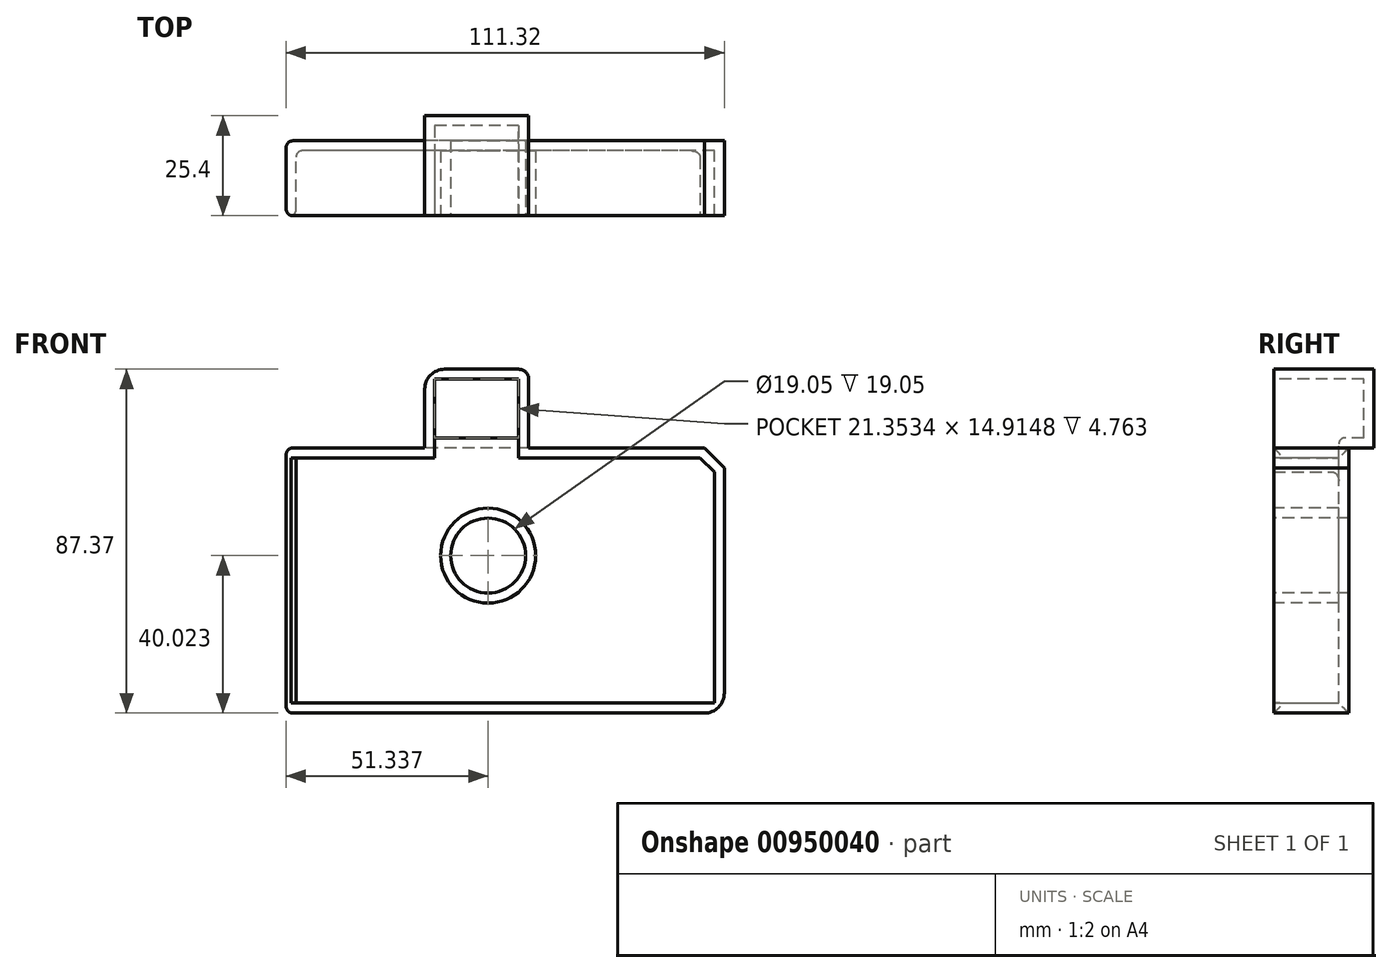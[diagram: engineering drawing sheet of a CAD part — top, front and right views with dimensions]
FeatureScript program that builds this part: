
annotation { "Feature Type Name" : "Feature", "Feature Type Description" : "" }
export const myFeature = defineFeature(function(context is Context, id is Id, definition is map)
    precondition{}
    {
        {
            var Q0;
            Q0=qCreatedBy(makeId("Front.planeOp"),FACE);
            var sketch = newSketch(context, id + "F0", { "sketchPlane" : qUnion([Q0])});
            skLineSegment(sketch, "E0.bottom", {"start": v(0, 21.6) * mm, "end": v(-111.32, 21.6) * mm});
            skLineSegment(sketch, "E0.top", {"start": v(0, 88.98) * mm, "end": v(-111.32, 88.98) * mm});
            skLineSegment(sketch, "E0.left", {"start": v(0, 21.6) * mm, "end": v(0, 88.98) * mm});
            skLineSegment(sketch, "E0.right", {"start": v(-111.32, 21.6) * mm, "end": v(-111.32, 88.98) * mm});
            skPoint(sketch, "E0.middle", {"position": v(-55.66, 55.3) * mm});
            skSolve(sketch);
        }
        {
            var Q0;
            Q0 = qSketchRegion(id + "F0", true);
            extrude(context, id + "F1", {"entities" : qUnion([Q0]), "depth" : 19.05 * mm, "offsetDistance" : 25.4 * mm});
        }
        {
            var Q0;
            Q0=makeQuery(id+"F1.opExtrude","CAP_FACE",FACE,{"disambiguationData":[OSD([sQuery(id+"F0.wireOp",EDGE,"E0.bottom"),sQuery(id+"F0.wireOp",EDGE,"E0.top"),sQuery(id+"F0.wireOp",EDGE,"E0.left"),sQuery(id+"F0.wireOp",EDGE,"E0.right")])],"isStart":false});
            var sketch = newSketch(context, id + "F2", { "sketchPlane" : qUnion([Q0])});
            skSolve(sketch);
        }
        {
            var Q0;
            Q0=makeQuery(id+"F1.opExtrude","SWEPT_FACE",FACE,{"disambiguationData":[OSD([sQuery(id+"F0.wireOp",EDGE,"E0.right")])]});
            fillet(context, id + "F3", {"entities" : qUnion([Q0]), "radius" : 1.73 * mm, "tangentPropagation" : true, "allowEdgeOverflow" : false});
        }
        {
            var Q0;
            Q0=makeQuery(id+"F2.imprint","IMPRINT",FACE,{"disambiguationData":[TD([[makeQuery(id+"F2.imprint","IMPRINT",EDGE,{"derivedFrom":makeQuery(id+"F1.opExtrude","CAP_EDGE",EDGE,{"disambiguationData":[OSD([sQuery(id+"F0.wireOp",EDGE,"E0.bottom")])],"isStart":false})}),-1.0]])]});
            var sketch = newSketch(context, id + "F4", { "sketchPlane" : qUnion([Q0])});
            skLineSegment(sketch, "E1.bottom", {"start": v(-76.1, 58.55) * mm, "end": v(-49.66, 58.55) * mm});
            skLineSegment(sketch, "E1.top", {"start": v(-76.1, 108.97) * mm, "end": v(-49.66, 108.97) * mm});
            skLineSegment(sketch, "E1.left", {"start": v(-76.1, 58.55) * mm, "end": v(-76.1, 108.97) * mm});
            skLineSegment(sketch, "E1.right", {"start": v(-49.66, 58.55) * mm, "end": v(-49.66, 108.97) * mm});
            skPoint(sketch, "E1.middle", {"position": v(-62.88, 83.76) * mm});
            skSolve(sketch);
        }
        {
            var Q0;
            {var subQ0=sQuery(id+"F4.wireOp",EDGE,"E1.top");Q0=makeQuery(id+"F4.imprint","IMPRINT",FACE,{"disambiguationData":[TD([[makeQuery(id+"F4.imprint","IMPRINT",EDGE,{"derivedFrom":subQ0}),-1.0]])]});}
            extrude(context, id + "F5", {"entities" : qUnion([Q0]), "oppositeDirection" : true, "depth" : 25.4 * mm, "offsetDistance" : 25.4 * mm});
        }
        {
            var Q0;
            Q0=makeQuery(id+"F1.opExtrude","SWEPT_BODY",BODY,{"disambiguationData":[OSD([sQuery(id+"F0.wireOp",EDGE,"E0.bottom"),sQuery(id+"F0.wireOp",EDGE,"E0.top"),sQuery(id+"F0.wireOp",EDGE,"E0.left"),sQuery(id+"F0.wireOp",EDGE,"E0.right")])]});
            var Q1;
            Q1=makeQuery(id+"F5.opExtrude","SWEPT_BODY",BODY,{"disambiguationData":[OSD([sQuery(id+"F0.wireOp",EDGE,"E0.top"),sQuery(id+"F4.wireOp",EDGE,"E1.top"),sQuery(id+"F4.wireOp",EDGE,"E1.left"),sQuery(id+"F4.wireOp",EDGE,"E1.right")])]});
            booleanBodies(context, id + "F6", {"operationType" : BooleanOperationType.UNION, "tools" : qUnion([Q0, Q1])});
        }
        {
            var Q0;
            Q0=makeQuery(id+"F2.imprint","IMPRINT",FACE,{"disambiguationData":[TD([[makeQuery(id+"F2.imprint","IMPRINT",EDGE,{"derivedFrom":makeQuery(id+"F1.opExtrude","CAP_EDGE",EDGE,{"disambiguationData":[OSD([sQuery(id+"F0.wireOp",EDGE,"E0.bottom")])],"isStart":false})}),-1.0]])]});
            var sketch = newSketch(context, id + "F7", { "sketchPlane" : qUnion([Q0])});
            skSolve(sketch);
        }
        {
            var Q0;
            Q0=makeQuery(id+"F1.opExtrude","SWEPT_EDGE",EDGE,{"disambiguationData":[OSD([sQuery(id+"F0.wireOp",EDGE,"E0.top"),sQuery(id+"F0.wireOp",EDGE,"E0.left")])]});
            chamfer(context, id + "F8", {"entities" : qUnion([Q0]), "width" : 5.08 * mm, "tangentPropagation" : true});
        }
        {
            var Q0;
            Q0=makeQuery(id+"F5.opExtrude","SWEPT_EDGE",EDGE,{"disambiguationData":[OSD([sQuery(id+"F4.wireOp",EDGE,"E1.top"),sQuery(id+"F4.wireOp",EDGE,"E1.right")])]});
            fillet(context, id + "F9", {"entities" : qUnion([Q0]), "radius" : 2.54 * mm, "tangentPropagation" : true, "allowEdgeOverflow" : false});
        }
        {
            var Q0;
            Q0=makeQuery(id+"F2.imprint","IMPRINT",FACE,{"disambiguationData":[TD([[makeQuery(id+"F2.imprint","IMPRINT",EDGE,{"derivedFrom":makeQuery(id+"F1.opExtrude","CAP_EDGE",EDGE,{"disambiguationData":[OSD([sQuery(id+"F0.wireOp",EDGE,"E0.bottom")])],"isStart":false})}),-1.0]])]});
            var sketch = newSketch(context, id + "F10", { "sketchPlane" : qUnion([Q0])});
            skCircle(sketch, "E2", {"center": v(-59.98, 61.62) * mm, "radius": 20.52 * mm});
            skSolve(sketch);
        }
        {
            var Q0;
            Q0=sQuery(id+"F10.wireOp",VERTEX,"E2.center");
            var Q1;
            Q1=makeQuery(id+"F1.opExtrude","SWEPT_BODY",BODY,{"disambiguationData":[OSD([sQuery(id+"F0.wireOp",EDGE,"E0.bottom"),sQuery(id+"F0.wireOp",EDGE,"E0.top"),sQuery(id+"F0.wireOp",EDGE,"E0.left"),sQuery(id+"F0.wireOp",EDGE,"E0.right")])]});
            hole(context, id + "F11", {"style" : HoleStyle.SIMPLE, "endStyle" : HoleEndStyle.THROUGH, "holeDiameter" : 19.05 * mm, "majorDiameter" : 6.35 * mm, "isTappedThrough" : true, "tappedDepth" : 12.7 * mm, "tapClearance" : 3, "locations" : qUnion([Q0]), "scope" : qUnion([Q1])});
        }
        {
            var Q0;
            {var subQ0=sQuery(id+"F0.wireOp",EDGE,"E0.top");Q0=makeQuery(id+"F6.opBoolean","MERGE",FACE,{"derivedFrom":[makeQuery(id+"F1.opExtrude","CAP_FACE",FACE,{"disambiguationData":[OSD([sQuery(id+"F0.wireOp",EDGE,"E0.bottom"),subQ0,sQuery(id+"F0.wireOp",EDGE,"E0.left"),sQuery(id+"F0.wireOp",EDGE,"E0.right")])],"isStart":false}),makeQuery(id+"F5.opExtrude","CAP_FACE",FACE,{"disambiguationData":[OSD([subQ0,sQuery(id+"F4.wireOp",EDGE,"E1.top"),sQuery(id+"F4.wireOp",EDGE,"E1.left"),sQuery(id+"F4.wireOp",EDGE,"E1.right")])],"isStart":true})]});}
            shell(context, id + "F12", {"entities" : qUnion([Q0]), "thickness" : 2.54 * mm});
        }
        {
            var Q0;
            Q0=makeQuery(id+"F12.opShell","OFFSET_EDGE",EDGE,{"disambiguationData":[OSD([sQuery(id+"F0.wireOp",EDGE,"E0.bottom"),sQuery(id+"F0.wireOp",EDGE,"E0.top"),sQuery(id+"F0.wireOp",EDGE,"E0.left"),sQuery(id+"F0.wireOp",EDGE,"E0.right"),sQuery(id+"F11.hole-0.sketch.wireOp",EDGE,"core_line_2")])]});
            fillet(context, id + "F13", {"entities" : qUnion([Q0]), "radius" : 1.59 * mm, "tangentPropagation" : true, "allowEdgeOverflow" : false});
        }
        {
            var Q0;
            Q0=makeQuery(id+"F5.opExtrude","SWEPT_EDGE",EDGE,{"disambiguationData":[OSD([sQuery(id+"F4.wireOp",EDGE,"E1.top"),sQuery(id+"F4.wireOp",EDGE,"E1.left")])]});
            fillet(context, id + "F14", {"entities" : qUnion([Q0]), "radius" : 5.08 * mm, "tangentPropagation" : true, "allowEdgeOverflow" : false});
        }
        {
            var Q0;
            Q0=makeQuery(id+"F1.opExtrude","SWEPT_EDGE",EDGE,{"disambiguationData":[OSD([sQuery(id+"F0.wireOp",EDGE,"E0.bottom"),sQuery(id+"F0.wireOp",EDGE,"E0.left")])]});
            fillet(context, id + "F15", {"entities" : qUnion([Q0]), "radius" : 5.08 * mm, "tangentPropagation" : true, "allowEdgeOverflow" : false});
        }
    });
